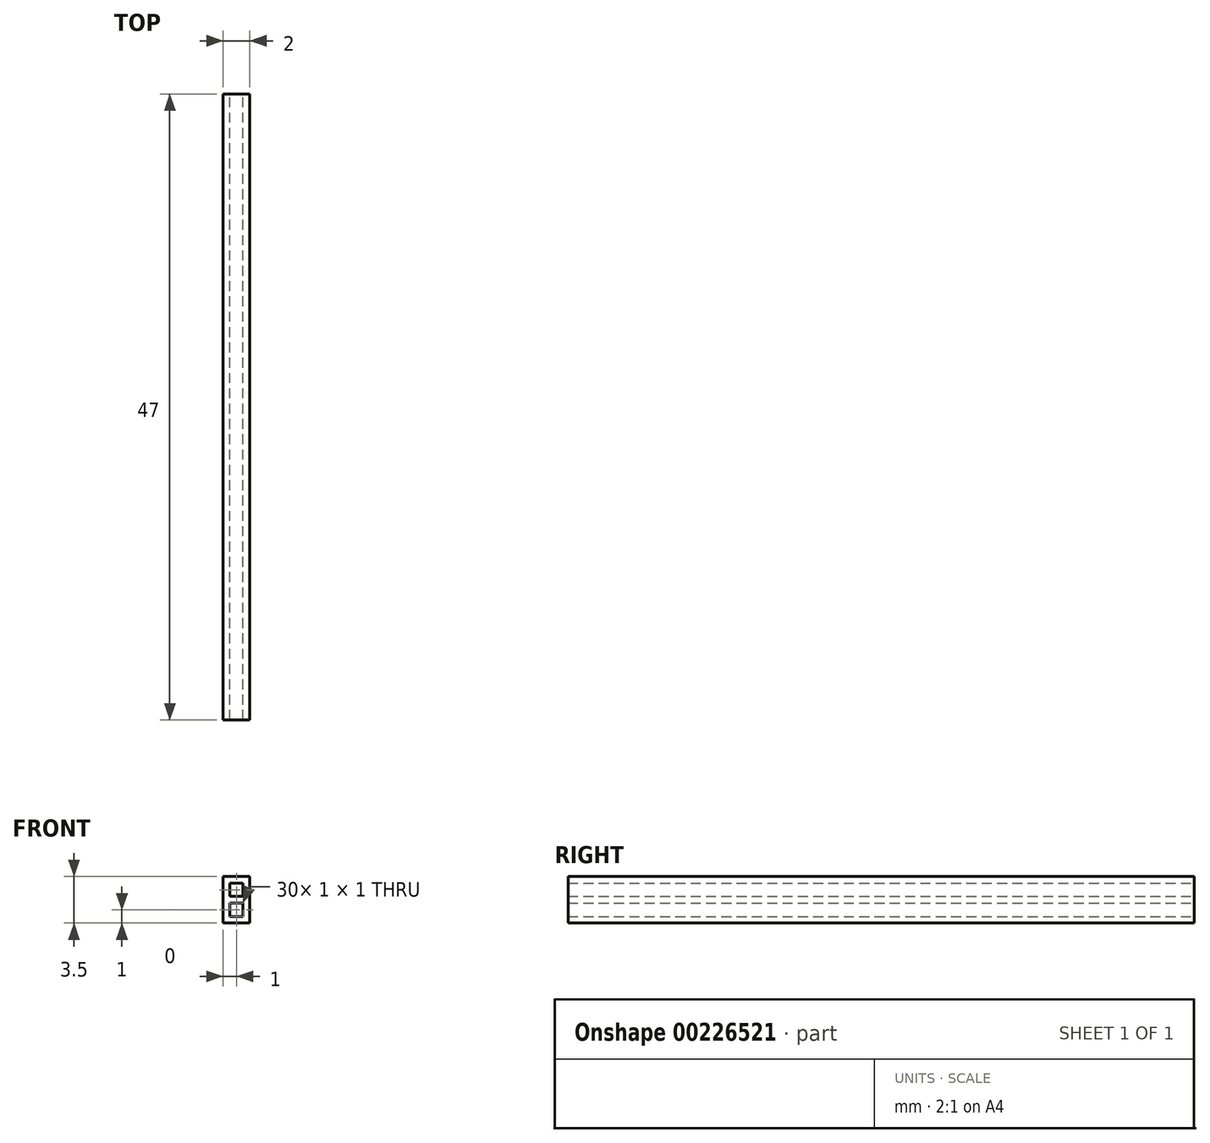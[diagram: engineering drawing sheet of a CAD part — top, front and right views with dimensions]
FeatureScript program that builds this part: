
annotation { "Feature Type Name" : "Feature", "Feature Type Description" : "" }
export const myFeature = defineFeature(function(context is Context, id is Id, definition is map)
    precondition{}
    {
        {
            var Q0;
            Q0=qCreatedBy(makeId("Front.planeOp"),FACE);
            var sketch = newSketch(context, id + "F0", { "sketchPlane" : qUnion([Q0])});
            skLineSegment(sketch, "E0.bottom", {"start": v(1, -1.75) * mm, "end": v(-1, -1.75) * mm});
            skLineSegment(sketch, "E0.top", {"start": v(1, 1.75) * mm, "end": v(-1, 1.75) * mm});
            skLineSegment(sketch, "E0.left", {"start": v(1, -1.75) * mm, "end": v(1, 1.75) * mm});
            skLineSegment(sketch, "E0.right", {"start": v(-1, -1.75) * mm, "end": v(-1, 1.75) * mm});
            skPoint(sketch, "E0.middle", {"position": v(0, 0) * mm});
            skLineSegment(sketch, "E1.bottom", {"start": v(0.5, 0.25) * mm, "end": v(-0.5, 0.25) * mm});
            skLineSegment(sketch, "E1.top", {"start": v(0.5, 1.25) * mm, "end": v(-0.5, 1.25) * mm});
            skLineSegment(sketch, "E1.left", {"start": v(0.5, 0.25) * mm, "end": v(0.5, 1.25) * mm});
            skLineSegment(sketch, "E1.right", {"start": v(-0.5, 0.25) * mm, "end": v(-0.5, 1.25) * mm});
            skLineSegment(sketch, "E2.MirrorCS", {"start": v(0.5, -0.25) * mm, "end": v(0.5, -1.25) * mm});
            skLineSegment(sketch, "E3.MirrorCS", {"start": v(0.5, -1.25) * mm, "end": v(-0.5, -1.25) * mm});
            skLineSegment(sketch, "E4.MirrorCS", {"start": v(-0.5, -0.25) * mm, "end": v(-0.5, -1.25) * mm});
            skLineSegment(sketch, "E5.MirrorCS", {"start": v(0.5, -0.25) * mm, "end": v(-0.5, -0.25) * mm});
            skSolve(sketch);
        }
        {
            var Q0;
            Q0=makeQuery(id+"F0.imprint","IMPRINT",FACE,{"disambiguationData":[TD([[makeQuery(id+"F0.imprint","IMPRINT",EDGE,{"derivedFrom":sQuery(id+"F0.wireOp",EDGE,"E0.bottom")}),-1.0]])]});
            extrude(context, id + "F1", {"entities" : qUnion([Q0]), "depth" : 47 * mm});
        }
    });
